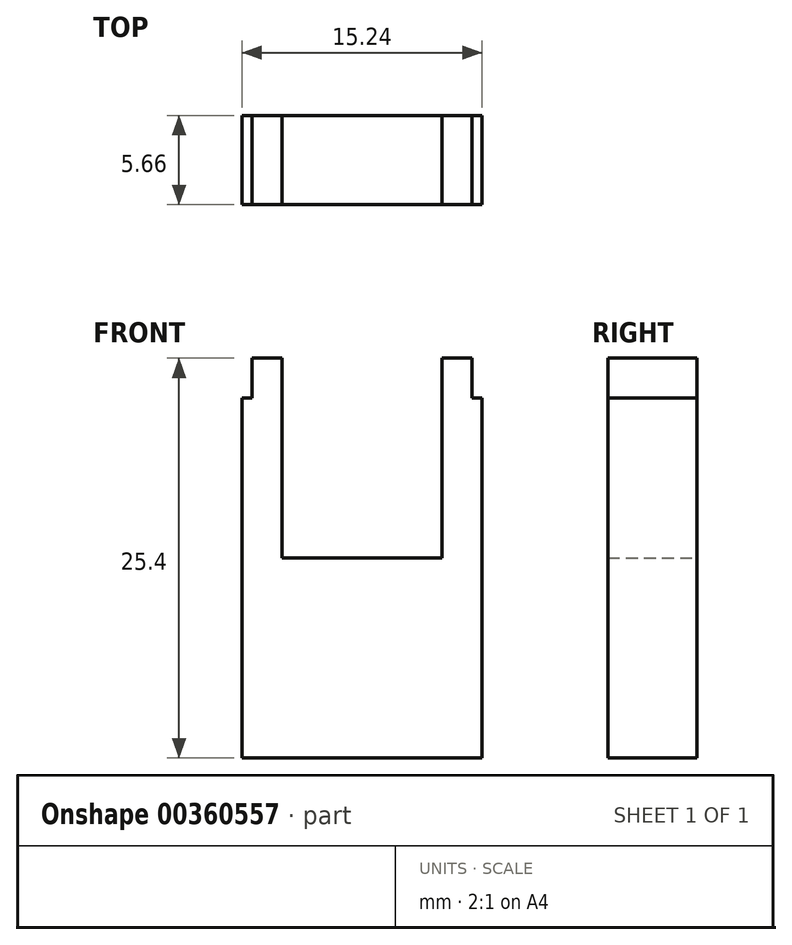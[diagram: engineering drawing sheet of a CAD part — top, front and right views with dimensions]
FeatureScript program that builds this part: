
annotation { "Feature Type Name" : "Feature", "Feature Type Description" : "" }
export const myFeature = defineFeature(function(context is Context, id is Id, definition is map)
    precondition{}
    {
        {
            var Q0;
            Q0=qCreatedBy(makeId("Front.planeOp"),FACE);
            var sketch = newSketch(context, id + "F0", { "sketchPlane" : qUnion([Q0])});
            skLineSegment(sketch, "E0.bottom", {"start": v(-7.62, 6.35) * mm, "end": v(7.62, 6.35) * mm});
            skLineSegment(sketch, "E0.top", {"start": v(-7.62, -6.35) * mm, "end": v(7.62, -6.35) * mm});
            skLineSegment(sketch, "E0.left", {"start": v(-7.62, 6.35) * mm, "end": v(-7.62, -6.35) * mm});
            skLineSegment(sketch, "E0.right", {"start": v(7.62, 6.35) * mm, "end": v(7.62, -6.35) * mm});
            skPoint(sketch, "E0.middle", {"position": v(0, 0) * mm});
            skLineSegment(sketch, "E1", {"start": v(-7.62, 6.35) * mm, "end": v(-7.62, 16.51) * mm});
            skLineSegment(sketch, "E2", {"start": v(7.62, 6.35) * mm, "end": v(7.62, 16.51) * mm});
            skLineSegment(sketch, "E3", {"start": v(-7.62, 16.51) * mm, "end": v(-5.08, 16.51) * mm});
            skLineSegment(sketch, "E4", {"start": v(5.08, 16.51) * mm, "end": v(7.62, 16.51) * mm});
            skLineSegment(sketch, "E5", {"start": v(-5.08, 16.51) * mm, "end": v(-5.08, 6.35) * mm});
            skLineSegment(sketch, "E6", {"start": v(-5.08, 16.51) * mm, "end": v(-5.08, 19.05) * mm});
            skLineSegment(sketch, "E7.0", {"start": v(-6.99, 16.51) * mm, "end": v(-6.99, 19.05) * mm});
            skLineSegment(sketch, "E8", {"start": v(-6.99, 19.05) * mm, "end": v(-5.08, 19.05) * mm});
            skLineSegment(sketch, "E9", {"start": v(5.08, 16.51) * mm, "end": v(5.08, 6.35) * mm});
            skLineSegment(sketch, "E10", {"start": v(5.08, 16.51) * mm, "end": v(5.08, 19.05) * mm});
            skLineSegment(sketch, "E11.0", {"start": v(6.98, 16.51) * mm, "end": v(6.98, 19.05) * mm});
            skLineSegment(sketch, "E12", {"start": v(5.08, 19.05) * mm, "end": v(6.98, 19.05) * mm});
            skSolve(sketch);
        }
        {
            var Q0;
            Q0 = qSketchRegion(id + "F0", true);
            extrude(context, id + "F1", {"entities" : qUnion([Q0]), "depth" : 5.66 * mm});
        }
    });
